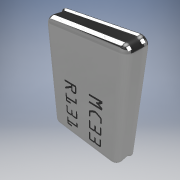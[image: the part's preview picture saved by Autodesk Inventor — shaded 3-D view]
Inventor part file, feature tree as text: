
AUTODESK INVENTOR PART (.ipt)
format: ipt  version: 2016 SP2 (Build 200237200, 237)  size: 653,824 bytes
history: native  units: in
note: dims shown in document units (in); Inventor stores cm internally (conversion verified against a paired STEP export)
features: extrude x1, sketch x1
ambient origin geometry x8: Origin, YZ Plane, XZ Plane, XY Plane, X Axis, Y Axis, Z Axis, Center Point
bodies: Solid1 (feature_tree)
feature tree (2):
  extrude  "Extrusion1"  [1 undecoded]
  sketch  "Sketch1"  dims[d0=0.0039in d1=0.0in]
note: 1 required parameter value undecoded (feature->parameter linkage not recoverable at this tier; creation-order binding heuristic only, values carry confidence <= 0.55)
